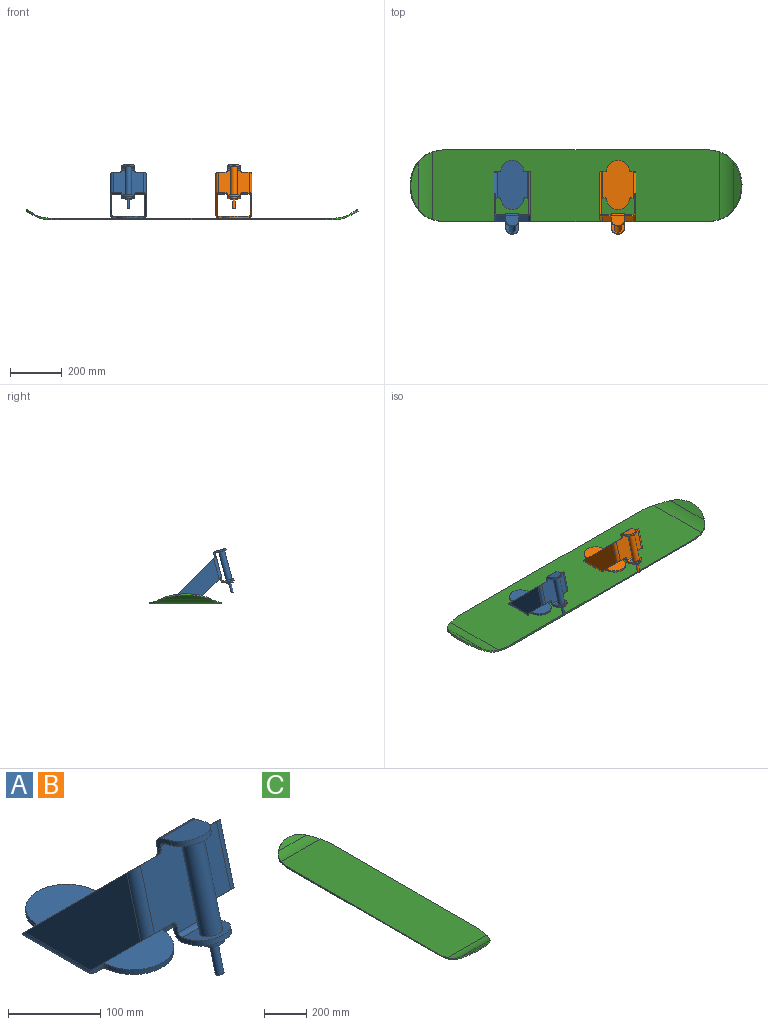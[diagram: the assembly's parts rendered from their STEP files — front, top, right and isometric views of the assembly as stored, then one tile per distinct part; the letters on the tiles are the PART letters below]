
ASSEMBLY  parts=3 mates=3
PART A: 53 faces, bbox 139.7x286.7x207.6 mm
  f0: plane 91.26x91.26mm, normal (0,-0.71,-0.71), area 1040.7mm2, adj f2,f8,f12,f14,f15,f16,f25,f26
  f1: plane 171.39x171.39mm, normal (0,0.71,0.71), area 1760.3mm2, adj f2,f7,f12,f14,f15,f16,f25,f26
  f2: plane 178.45x156.98mm, normal (1,0,0), area 11878.5mm2, adj f0,f1,f15,f26
  f3: cylinder r=44.45mm len=88.43mm, axis (0,0,-1), area 828.7mm2, adj f5,f6,f9,f19
  f4: cylinder r=44.45mm len=88.43mm, axis (0,0,-1), area 828.7mm2, adj f5,f6,f10,f20
  f5: plane 190.5x116.84mm, normal (0,0,1), area 18096.9mm2, adj f3,f4,f7,f8,f9,f10,f15,f17
  f6: plane 190.5x116.84mm, normal (0,0,-1), area 18096.9mm2, adj f3,f4,f7,f8,f9,f10,f16,f17
  f7: plane 19.39x6.35mm, normal (0,1,0), area 104.6mm2, adj f1,f5,f6,f9,f16
  f8: plane 19.39x6.35mm, normal (0,-1,0), area 104.6mm2, adj f0,f5,f6,f10,f16
  f9: cylinder r=5.08mm len=6.35mm, axis (0,0,-1), area 47.4mm2, adj f3,f5,f6,f7
  f10: cylinder r=5.08mm len=6.35mm, axis (0,0,-1), area 47.4mm2, adj f4,f5,f6,f8
  f11: plane 91.26x91.26mm, normal (0,-0.71,-0.71), area 1040.7mm2, adj f12,f18,f21,f22,f23,f24,f25,f27
  f12: plane 116.84x100.59mm, normal (0,-0.97,0.26), area 10794.3mm2, adj f0,f1,f11,f13,f28,f29,f32,f33
  f13: plane 171.39x171.39mm, normal (0,0.71,0.71), area 1760.3mm2, adj f12,f17,f21,f22,f23,f24,f25,f27
  f14: plane 178.45x156.98mm, normal (-1,0,0), area 11878.5mm2, adj f0,f1,f16,f29
  f15: cylinder r=5.08mm len=106.68mm, axis (0,-1,0), area 810.7mm2, adj f0,f1,f2,f5
  f16: cylinder r=11.43mm len=106.68mm, axis (0,1,0), area 1824.1mm2, adj f0,f1,f6,f7,f8,f14
  f17: plane 19.39x6.35mm, normal (0,1,0), area 104.6mm2, adj f5,f6,f13,f19,f24
  f18: plane 19.39x6.35mm, normal (0,-1,0), area 104.6mm2, adj f5,f6,f11,f20,f24
  f19: cylinder r=5.08mm len=6.35mm, axis (0,0,-1), area 47.4mm2, adj f3,f5,f6,f17
  f20: cylinder r=5.08mm len=6.35mm, axis (0,0,-1), area 47.4mm2, adj f4,f5,f6,f18
  f21: plane 178.45x156.98mm, normal (1,0,0), area 11878.5mm2, adj f11,f13,f24,f28
  f22: plane 178.45x156.98mm, normal (-1,0,0), area 11878.5mm2, adj f11,f13,f23,f27
  f23: cylinder r=5.08mm len=106.68mm, axis (0,-1,0), area 810.7mm2, adj f5,f11,f13,f22
  f24: cylinder r=11.43mm len=106.68mm, axis (0,1,0), area 1824.1mm2, adj f6,f11,f13,f17,f18,f21
  f25: plane 116.84x100.59mm, normal (0,0.97,-0.26), area 10794.3mm2, adj f0,f1,f11,f13,f26,f27,f32,f33
  f26: cylinder r=5.08mm len=84.28mm, axis (0,-0.26,-0.97), area 662mm2, adj f0,f1,f2,f25
  f27: cylinder r=5.08mm len=84.28mm, axis (0,-0.26,-0.97), area 662mm2, adj f11,f13,f22,f25
  f28: cylinder r=11.43mm len=89.46mm, axis (0,-0.26,-0.97), area 1489.4mm2, adj f11,f12,f13,f21
  f29: cylinder r=11.43mm len=89.46mm, axis (0,-0.26,-0.97), area 1489.4mm2, adj f0,f1,f12,f14
  f30: plane 50.8x38.03mm, normal (0,0.26,0.97), area 1723.1mm2, adj f32,f33,f45,f52
  f31: plane 50.8x38.03mm, normal (0,-0.26,-0.97), area 1216.4mm2, adj f32,f33,f41,f48,f52
  f32: plane 23.61x22.85mm, normal (1,0,0), area 193.8mm2, adj f12,f25,f30,f31,f41,f43,f45,f52
  f33: plane 23.61x22.85mm, normal (-1,0,0), area 193.8mm2, adj f12,f25,f30,f31,f41,f42,f45,f52
  f34: plane 50.8x38.03mm, normal (0,0.26,0.97), area 1216.4mm2, adj f36,f37,f38,f48,f51
  f35: plane 50.8x38.03mm, normal (0,-0.26,-0.97), area 1216.4mm2, adj f36,f37,f44,f47,f51
  f36: plane 28.54x17.55mm, normal (1,0,0), area 208.3mm2, adj f12,f25,f34,f35,f38,f40,f44,f51
  f37: plane 28.54x17.55mm, normal (-1,0,0), area 208.3mm2, adj f12,f25,f34,f35,f38,f39,f44,f51
  f38: cylinder r=5.08mm len=50.8mm, axis (-1,0,0), area 405.4mm2, adj f12,f34,f36,f37
  f39: cylinder r=5.08mm len=10.85mm, axis (0,-0.71,0.71), area 58.5mm2, adj f0,f12,f25,f37
  f40: cylinder r=5.08mm len=10.85mm, axis (0,0.71,-0.71), area 58.5mm2, adj f11,f12,f25,f36
  f41: cylinder r=5.08mm len=50.8mm, axis (-1,0,0), area 405.4mm2, adj f12,f31,f32,f33
  f42: cylinder r=5.08mm len=10.85mm, axis (0,0.71,-0.71), area 58.5mm2, adj f1,f12,f25,f33
  f43: cylinder r=5.08mm len=10.85mm, axis (0,-0.71,0.71), area 58.5mm2, adj f12,f13,f25,f32
  f44: cylinder r=11.43mm len=50.8mm, axis (-1,0,0), area 912.1mm2, adj f25,f35,f36,f37
  f45: cylinder r=11.43mm len=50.8mm, axis (-1,0,0), area 912.1mm2, adj f25,f30,f32,f33
  f46: plane 25.4x24.53mm, normal (0,-0.26,-0.97), area 435.5mm2, adj f47,f49
  f47: cylinder r=12.7mm len=26.18mm, axis (0,0.26,0.97), area 506.7mm2, adj f35,f46
  f48: cylinder r=12.7mm len=116.98mm, axis (0,0.26,0.97), area 9120.7mm2, adj f31,f34
  f49: cylinder r=4.76mm len=39.27mm, axis (0,0.26,0.97), area 1140.1mm2, adj f46,f50
  f50: plane 9.53x9.2mm, normal (0,-0.26,-0.97), area 71.3mm2, adj f49
  f51: cylinder r=25.4mm len=50.8mm, axis (0,0.26,0.97), area 506.7mm2, adj f34,f35,f36,f37
  f52: cylinder r=25.4mm len=50.8mm, axis (0,0.26,0.97), area 506.7mm2, adj f30,f31,f32,f33
PART B: same geometry as A
PART C: 14 faces, bbox 279.4x1284.7x113.5 mm
  f0: plane 189.76x32.42mm, normal (0,-0.49,-0.87), area 4842.9mm2, adj f7,f8
  f1: plane 1109.37x279.4mm, normal (0,0,-1), area 309358.2mm2, adj f4,f5,f7,f8,f12,f13
  f2: plane 1111.23x279.4mm, normal (0,0,1), area 309711.5mm2, adj f4,f5,f6,f8,f11,f13
  f3: plane 184.78x30.24mm, normal (0,0.5,0.87), area 4421.6mm2, adj f6,f8
  f4: plane 999.76x6.35mm, normal (1,0,0), area 6325.2mm2, adj f1,f2,f8,f13
  f5: plane 999.76x6.35mm, normal (-1,0,0), area 6325.2mm2, adj f1,f2,f8,f13
  f6: cylinder r=106.68mm len=259.77mm, axis (1,0,0), area 12814.2mm2, adj f2,f3,f8
  f7: cylinder r=113.03mm len=262.78mm, axis (-1,0,0), area 13478.7mm2, adj f0,f1,f8
  f8: cylinder r=139.7mm len=279.4mm, axis (0,0.5,0.87), area 2857mm2, adj f0,f1,f2,f3,f4,f5,f6,f7
  f9: plane 189.76x32.42mm, normal (0,0.49,-0.87), area 4842.9mm2, adj f12,f13
  f10: plane 184.78x30.24mm, normal (0,-0.5,0.87), area 4421.6mm2, adj f11,f13
  f11: cylinder r=106.68mm len=259.77mm, axis (1,0,0), area 12814.2mm2, adj f2,f10,f13
  f12: cylinder r=113.03mm len=262.78mm, axis (-1,0,0), area 13478.7mm2, adj f1,f9,f13
  f13: cylinder r=139.7mm len=279.4mm, axis (0,-0.5,0.87), area 2857mm2, adj f1,f2,f4,f5,f9,f10,f11,f12
PLACE A t=(-247.6,108.5,-592.67)mm
PLACE B rot(axis=(0,0,-1),0deg) t=(161.01,108.5,-592.67)mm
PLACE C rot(axis=(0,0,-1),90deg) t=(-1.13,104.87,-599.02)mm
MATE planar A.f25 <-> B.f25  axis (0,0.97,-0.26) through (-247.6,-17.55,-459.85)mm
MATE planar A.f6 <-> C.f2  axis (0,0,-1) through (-247.6,108.5,-592.67)mm
MATE planar B.f6 <-> A.f4  axis (0,0,-1) through (161.01,108.5,-592.67)mm
